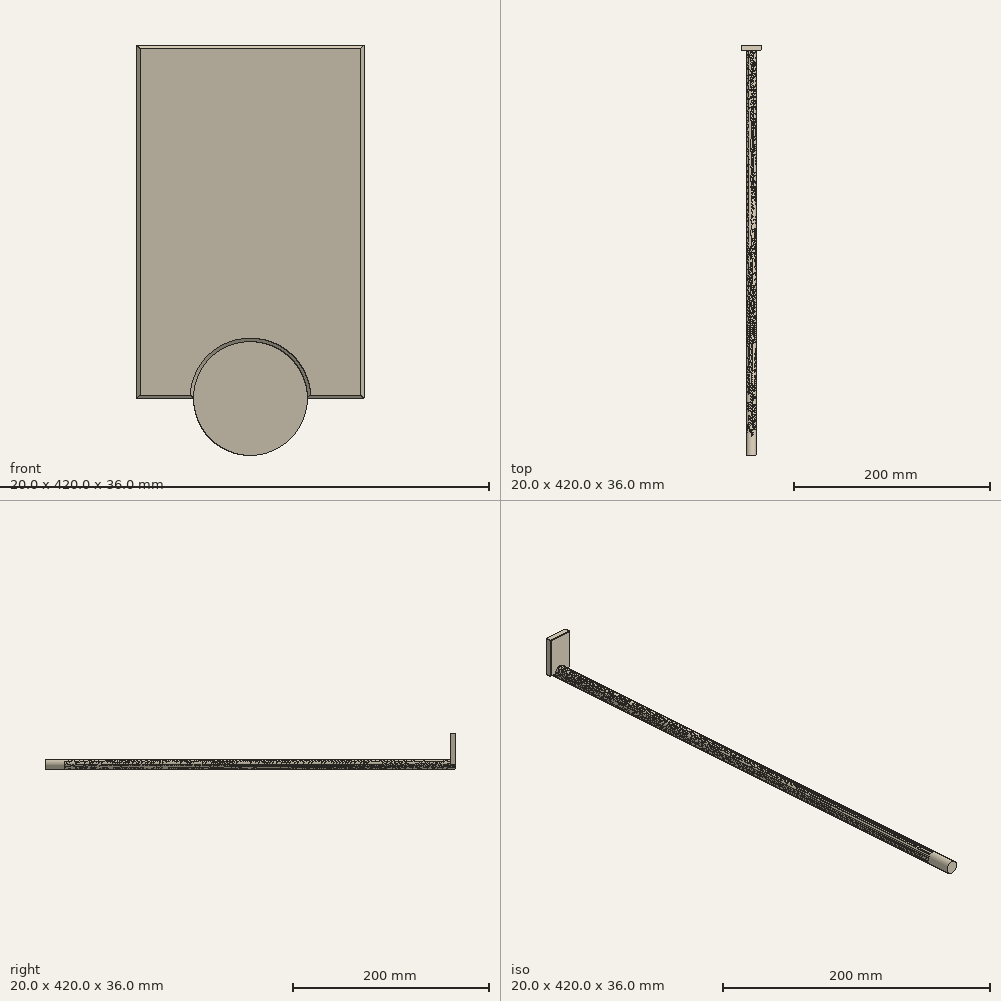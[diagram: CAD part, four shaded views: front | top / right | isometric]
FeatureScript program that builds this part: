
annotation { "Feature Type Name" : "Feature", "Feature Type Description" : "" }
export const myFeature = defineFeature(function(context is Context, id is Id, definition is map)
    precondition{}
    {
        {
            var Q0;
            Q0=qCreatedBy(makeId("Front.planeOp"),FACE);
            var sketch = newSketch(context, id + "F0", { "sketchPlane" : qUnion([Q0])});
            skLineSegment(sketch, "E0", {"start": v(50, 0) * mm, "end": v(-50, 0) * mm, "construction": true});
            skLineSegment(sketch, "E1", {"start": v(0, 50) * mm, "end": v(0, -50) * mm, "construction": true});
            skCircle(sketch, "E2", {"center": v(0, 0) * mm, "radius": 5 * mm});
            skSolve(sketch);
        }
        {
            var Q0;
            Q0 = qSketchRegion(id + "F0", true);
            var Q1;
            Q1=makeQuery(id+"F0.imprint","IMPRINT",FACE,{"disambiguationData":[TD([[makeQuery(id+"F0.imprint","IMPRINT",EDGE,{"derivedFrom":sQuery(id+"F0.wireOp",EDGE,"E2")}),1.0]])]});
            extrude(context, id + "F1", {"entities" : qUnion([Q0, Q1]), "depth" : 400 * mm, "offsetDistance" : 25 * mm});
        }
        {
            var Q0;
            Q0=qCreatedBy(makeId("Front.planeOp"),FACE);
            var sketch = newSketch(context, id + "F2", { "sketchPlane" : qUnion([Q0])});
            skLineSegment(sketch, "E3.bottom", {"start": v(-10, 31) * mm, "end": v(10, 31) * mm});
            skLineSegment(sketch, "E3.top", {"start": v(-10, 0) * mm, "end": v(-5, 0) * mm});
            skLineSegment(sketch, "E3.left", {"start": v(-10, 31) * mm, "end": v(-10, 0) * mm});
            skLineSegment(sketch, "E3.right", {"start": v(10, 31) * mm, "end": v(10, 0) * mm});
            skArc(sketch, "E4", {"start": v(5, 0) * mm, "mid": v(0, 5) * mm, "end": v(-5, 0) * mm});
            skLineSegment(sketch, "E5.trimOffspring", {"start": v(5, 0) * mm, "end": v(10, 0) * mm});
            skText(sketch, "E6", { "text": "31MM", "fontName": "OpenSans-Bold.ttf"});
            skPoint(sketch, "E7", {"position": v(0, 30) * mm});
            skLineSegment(sketch, "E8", {"start": v(0, 0) * mm, "end": v(0, 31) * mm, "construction": true});
            const initialGuessF2  = {"E6": [0.00228, 0.011, 0, 1, 0.00456]};
            skSetInitialGuess(sketch, initialGuessF2);
            skSolve(sketch);
        }
        {
            var Q0;
            Q0=makeQuery(id+"F2.imprint","IMPRINT",FACE,{"disambiguationData":[TD([[makeQuery(id+"F2.imprint","IMPRINT",EDGE,{"derivedFrom":sQuery(id+"F2.wireOp",EDGE,"E6.sketch_text.stroke-0")}),-1.0]])]});
            var Q1;
            Q1=makeQuery(id+"F2.imprint","IMPRINT",FACE,{"disambiguationData":[TD([[makeQuery(id+"F2.imprint","IMPRINT",EDGE,{"derivedFrom":sQuery(id+"F2.wireOp",EDGE,"E6.sketch_text.stroke-27")}),-1.0]])]});
            var Q2;
            Q2=makeQuery(id+"F2.imprint","IMPRINT",FACE,{"disambiguationData":[TD([[makeQuery(id+"F2.imprint","IMPRINT",EDGE,{"derivedFrom":sQuery(id+"F2.wireOp",EDGE,"E6.sketch_text.stroke-37")}),-1.0]])]});
            var Q3;
            Q3=makeQuery(id+"F2.imprint","IMPRINT",FACE,{"disambiguationData":[TD([[makeQuery(id+"F2.imprint","IMPRINT",EDGE,{"derivedFrom":sQuery(id+"F2.wireOp",EDGE,"E6.sketch_text.stroke-56")}),-1.0]])]});
            var Q4;
            Q4=makeQuery(id+"F2.imprint","IMPRINT",FACE,{"disambiguationData":[TD([[makeQuery(id+"F2.imprint","IMPRINT",EDGE,{"derivedFrom":sQuery(id+"F2.wireOp",EDGE,"E3.bottom")}),-1.0]])]});
            extrude(context, id + "F3", {"entities" : qUnion([Q0, Q1, Q2, Q3, Q4]), "depth" : 5 * mm, "offsetDistance" : 25 * mm});
        }
        {
            var Q0;
            Q0=makeQuery(id+"F3.opExtrude","CAP_FACE",FACE,{"disambiguationData":[OSD([sQuery(id+"F2.wireOp",EDGE,"E3.bottom"),sQuery(id+"F2.wireOp",EDGE,"E3.top"),sQuery(id+"F2.wireOp",EDGE,"E3.left"),sQuery(id+"F2.wireOp",EDGE,"E3.right"),sQuery(id+"F2.wireOp",EDGE,"E4"),sQuery(id+"F2.wireOp",EDGE,"E5.trimOffspring")])],"isStart":false});
            var Q1;
            Q1=makeQuery(id+"F3.opExtrude","CAP_FACE",FACE,{"disambiguationData":[OSD([sQuery(id+"F2.wireOp",EDGE,"E3.bottom"),sQuery(id+"F2.wireOp",EDGE,"E3.top"),sQuery(id+"F2.wireOp",EDGE,"E3.left"),sQuery(id+"F2.wireOp",EDGE,"E3.right"),sQuery(id+"F2.wireOp",EDGE,"E4"),sQuery(id+"F2.wireOp",EDGE,"E5.trimOffspring")])],"isStart":true});
            chamfer(context, id + "F4", {"entities" : qUnion([Q0, Q1]), "width" : 0.3 * mm, "tangentPropagation" : true});
        }
        {
            var Q0;
            Q0=makeQuery(id+"F2.imprint","IMPRINT",FACE,{"disambiguationData":[TD([[makeQuery(id+"F2.imprint","IMPRINT",EDGE,{"derivedFrom":sQuery(id+"F2.wireOp",EDGE,"E6.sketch_text.stroke-31")}),-1.0]])]});
            var Q1;
            Q1=makeQuery(id+"F2.imprint","IMPRINT",FACE,{"disambiguationData":[TD([[makeQuery(id+"F2.imprint","IMPRINT",EDGE,{"derivedFrom":sQuery(id+"F2.wireOp",EDGE,"E6.sketch_text.stroke-50")}),-1.0]])]});
            var Q2;
            Q2=makeQuery(id+"F2.imprint","IMPRINT",FACE,{"disambiguationData":[TD([[makeQuery(id+"F2.imprint","IMPRINT",EDGE,{"derivedFrom":sQuery(id+"F2.wireOp",EDGE,"E6.sketch_text.stroke-24")}),-1.0]])]});
            var Q3;
            Q3=makeQuery(id+"F2.imprint","IMPRINT",FACE,{"disambiguationData":[TD([[makeQuery(id+"F2.imprint","IMPRINT",EDGE,{"derivedFrom":sQuery(id+"F2.wireOp",EDGE,"E6.sketch_text.stroke-0")}),-1.0]])]});
            var Q4;
            Q4=makeQuery(id+"F2.imprint","IMPRINT",FACE,{"disambiguationData":[TD([[makeQuery(id+"F2.imprint","IMPRINT",EDGE,{"derivedFrom":sQuery(id+"F2.wireOp",EDGE,"E6.sketch_text.stroke-56")}),-1.0]])]});
            extrude(context, id + "F5", {"entities" : qUnion([Q0, Q1, Q2, Q3, Q4]), "operationType" : NewBodyOperationType.REMOVE, "depth" : 0.5 * mm, "offsetDistance" : 25 * mm});
        }
        {
            var Q0;
            Q0 = qSketchRegion(id + "F0", true);
            extrude(context, id + "F6", {"entities" : qUnion([Q0]), "depth" : 420 * mm, "offsetDistance" : 25 * mm});
        }
    });
